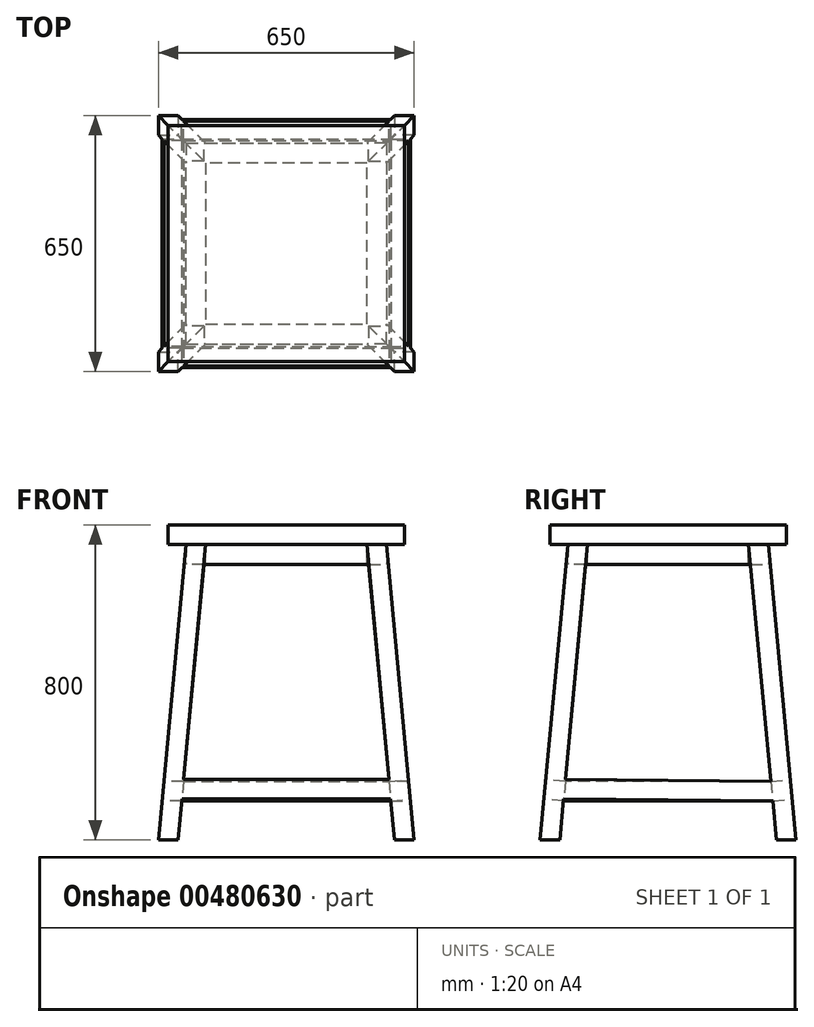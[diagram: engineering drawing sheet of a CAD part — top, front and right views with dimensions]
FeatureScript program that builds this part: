
annotation { "Feature Type Name" : "Feature", "Feature Type Description" : "" }
export const myFeature = defineFeature(function(context is Context, id is Id, definition is map)
    precondition{}
    {
        {
            var Q0;
            Q0=qCreatedBy(makeId("Top.planeOp"),FACE);
            var sketch = newSketch(context, id + "F0", { "sketchPlane" : qUnion([Q0])});
            skLineSegment(sketch, "E0.bottom", {"start": v(-250, 250) * mm, "end": v(250, 250) * mm, "construction": true});
            skLineSegment(sketch, "E0.top", {"start": v(-250, -250) * mm, "end": v(250, -250) * mm, "construction": true});
            skLineSegment(sketch, "E0.left", {"start": v(-250, 250) * mm, "end": v(-250, -250) * mm, "construction": true});
            skLineSegment(sketch, "E0.right", {"start": v(250, 250) * mm, "end": v(250, -250) * mm, "construction": true});
            skPoint(sketch, "E0.middle", {"position": v(0, 0) * mm});
            skLineSegment(sketch, "E1.bottom", {"start": v(-250, -250) * mm, "end": v(-200, -250) * mm});
            skLineSegment(sketch, "E1.top", {"start": v(-250, -200) * mm, "end": v(-200, -200) * mm});
            skLineSegment(sketch, "E1.left", {"start": v(-250, -250) * mm, "end": v(-250, -200) * mm});
            skLineSegment(sketch, "E1.right", {"start": v(-200, -250) * mm, "end": v(-200, -200) * mm});
            skLineSegment(sketch, "E2.bottom", {"start": v(250, -250) * mm, "end": v(200, -250) * mm});
            skLineSegment(sketch, "E2.top", {"start": v(250, -200) * mm, "end": v(200, -200) * mm});
            skLineSegment(sketch, "E2.left", {"start": v(250, -250) * mm, "end": v(250, -200) * mm});
            skLineSegment(sketch, "E2.right", {"start": v(200, -250) * mm, "end": v(200, -200) * mm});
            skLineSegment(sketch, "E3.bottom", {"start": v(250, 250) * mm, "end": v(200, 250) * mm});
            skLineSegment(sketch, "E3.top", {"start": v(250, 200) * mm, "end": v(200, 200) * mm});
            skLineSegment(sketch, "E3.left", {"start": v(250, 250) * mm, "end": v(250, 200) * mm});
            skLineSegment(sketch, "E3.right", {"start": v(200, 250) * mm, "end": v(200, 200) * mm});
            skLineSegment(sketch, "E4.bottom", {"start": v(-250, 250) * mm, "end": v(-200, 250) * mm});
            skLineSegment(sketch, "E4.top", {"start": v(-250, 200) * mm, "end": v(-200, 200) * mm});
            skLineSegment(sketch, "E4.left", {"start": v(-250, 250) * mm, "end": v(-250, 200) * mm});
            skLineSegment(sketch, "E4.right", {"start": v(-200, 250) * mm, "end": v(-200, 200) * mm});
            skSolve(sketch);
        }
        {
            var Q0;
            Q0=qCreatedBy(makeId("Top.planeOp"),FACE);
            cPlane(context, id + "F1", {"entities" : qUnion([Q0]), "cplaneType" : CPlaneType.OFFSET, "offset" : 800 * mm, "oppositeDirection" : true, "width" : 150 * mm, "height" : 150 * mm});
        }
        {
            var Q0;
            Q0=qCreatedBy(id+"F1.planeOp",FACE);
            var sketch = newSketch(context, id + "F2", { "sketchPlane" : qUnion([Q0])});
            skLineSegment(sketch, "E5.bottom", {"start": v(-325, 325) * mm, "end": v(325, 325) * mm, "construction": true});
            skLineSegment(sketch, "E5.top", {"start": v(-325, -325) * mm, "end": v(325, -325) * mm, "construction": true});
            skLineSegment(sketch, "E5.left", {"start": v(-325, 325) * mm, "end": v(-325, -325) * mm, "construction": true});
            skLineSegment(sketch, "E5.right", {"start": v(325, 325) * mm, "end": v(325, -325) * mm, "construction": true});
            skPoint(sketch, "E5.middle", {"position": v(0, 0) * mm});
            skLineSegment(sketch, "E6.bottom", {"start": v(-325, -325) * mm, "end": v(-275, -325) * mm});
            skLineSegment(sketch, "E6.top", {"start": v(-325, -275) * mm, "end": v(-275, -275) * mm});
            skLineSegment(sketch, "E6.left", {"start": v(-325, -325) * mm, "end": v(-325, -275) * mm});
            skLineSegment(sketch, "E6.right", {"start": v(-275, -325) * mm, "end": v(-275, -275) * mm});
            skLineSegment(sketch, "E7.bottom", {"start": v(325, -325) * mm, "end": v(275, -325) * mm});
            skLineSegment(sketch, "E7.top", {"start": v(325, -275) * mm, "end": v(275, -275) * mm});
            skLineSegment(sketch, "E7.left", {"start": v(325, -325) * mm, "end": v(325, -275) * mm});
            skLineSegment(sketch, "E7.right", {"start": v(275, -325) * mm, "end": v(275, -275) * mm});
            skLineSegment(sketch, "E8.bottom", {"start": v(325, 325) * mm, "end": v(275, 325) * mm});
            skLineSegment(sketch, "E8.top", {"start": v(325, 275) * mm, "end": v(275, 275) * mm});
            skLineSegment(sketch, "E8.left", {"start": v(325, 325) * mm, "end": v(325, 275) * mm});
            skLineSegment(sketch, "E8.right", {"start": v(275, 325) * mm, "end": v(275, 275) * mm});
            skLineSegment(sketch, "E9.bottom", {"start": v(-325, 325) * mm, "end": v(-275, 325) * mm});
            skLineSegment(sketch, "E9.top", {"start": v(-325, 275) * mm, "end": v(-275, 275) * mm});
            skLineSegment(sketch, "E9.left", {"start": v(-325, 325) * mm, "end": v(-325, 275) * mm});
            skLineSegment(sketch, "E9.right", {"start": v(-275, 325) * mm, "end": v(-275, 275) * mm});
            skSolve(sketch);
        }
        {
            var Q0;
            Q0=qCreatedBy(makeId("Top.planeOp"),FACE);
            var sketch = newSketch(context, id + "F3", { "sketchPlane" : qUnion([Q0])});
            skLineSegment(sketch, "E10.bottom", {"start": v(-300, 300) * mm, "end": v(300, 300) * mm});
            skLineSegment(sketch, "E10.top", {"start": v(-300, -300) * mm, "end": v(300, -300) * mm});
            skLineSegment(sketch, "E10.left", {"start": v(-300, 300) * mm, "end": v(-300, -300) * mm});
            skLineSegment(sketch, "E10.right", {"start": v(300, 300) * mm, "end": v(300, -300) * mm});
            skPoint(sketch, "E10.middle", {"position": v(0, 0) * mm});
            skSolve(sketch);
        }
        {
            var Q0;
            Q0=makeQuery(id+"F0.imprint","IMPRINT",FACE,{"disambiguationData":[TD([[makeQuery(id+"F0.imprint","IMPRINT",EDGE,{"derivedFrom":sQuery(id+"F0.wireOp",EDGE,"E1.bottom")}),1.0]])]});
            var Q1;
            Q1=makeQuery(id+"F2.imprint","IMPRINT",FACE,{"disambiguationData":[TD([[makeQuery(id+"F2.imprint","IMPRINT",EDGE,{"derivedFrom":sQuery(id+"F2.wireOp",EDGE,"E6.bottom")}),1.0]])]});
            loft(context, id + "F4", {"sheetProfilesArray" : [{ "sheetProfileEntities" : qUnion([Q0]) }, { "sheetProfileEntities" : qUnion([Q1]) }]});
        }
        {
            var Q0;
            Q0=makeQuery(id+"F0.imprint","IMPRINT",FACE,{"disambiguationData":[TD([[makeQuery(id+"F0.imprint","IMPRINT",EDGE,{"derivedFrom":sQuery(id+"F0.wireOp",EDGE,"E2.bottom")}),-1.0]])]});
            var Q1;
            Q1=makeQuery(id+"F2.imprint","IMPRINT",FACE,{"disambiguationData":[TD([[makeQuery(id+"F2.imprint","IMPRINT",EDGE,{"derivedFrom":sQuery(id+"F2.wireOp",EDGE,"E7.bottom")}),-1.0]])]});
            loft(context, id + "F5", {"sheetProfilesArray" : [{ "sheetProfileEntities" : qUnion([Q0]) }, { "sheetProfileEntities" : qUnion([Q1]) }]});
        }
        {
            var Q0;
            Q0=makeQuery(id+"F0.imprint","IMPRINT",FACE,{"disambiguationData":[TD([[makeQuery(id+"F0.imprint","IMPRINT",EDGE,{"derivedFrom":sQuery(id+"F0.wireOp",EDGE,"E4.bottom")}),-1.0]])]});
            var Q1;
            Q1=makeQuery(id+"F2.imprint","IMPRINT",FACE,{"disambiguationData":[TD([[makeQuery(id+"F2.imprint","IMPRINT",EDGE,{"derivedFrom":sQuery(id+"F2.wireOp",EDGE,"E9.bottom")}),-1.0]])]});
            loft(context, id + "F6", {"sheetProfilesArray" : [{ "sheetProfileEntities" : qUnion([Q0]) }, { "sheetProfileEntities" : qUnion([Q1]) }]});
        }
        {
            var Q0;
            Q0=makeQuery(id+"F0.imprint","IMPRINT",FACE,{"disambiguationData":[TD([[makeQuery(id+"F0.imprint","IMPRINT",EDGE,{"derivedFrom":sQuery(id+"F0.wireOp",EDGE,"E3.bottom")}),1.0]])]});
            var Q1;
            Q1=makeQuery(id+"F2.imprint","IMPRINT",FACE,{"disambiguationData":[TD([[makeQuery(id+"F2.imprint","IMPRINT",EDGE,{"derivedFrom":sQuery(id+"F2.wireOp",EDGE,"E8.bottom")}),1.0]])]});
            loft(context, id + "F7", {"sheetProfilesArray" : [{ "sheetProfileEntities" : qUnion([Q0]) }, { "sheetProfileEntities" : qUnion([Q1]) }]});
        }
        {
            var Q0;
            Q0=qSketchRegion(id+"F3",true);
            extrude(context, id + "F8", {"entities" : qUnion([Q0]), "operationType" : NewBodyOperationType.ADD, "oppositeDirection" : true, "depth" : 50 * mm});
        }
        {
            var Q0;
            Q0=makeQuery(id+"F8.opExtrude","CAP_FACE",FACE,{"disambiguationData":[OSD([sQuery(id+"F3.wireOp",EDGE,"E10.bottom"),sQuery(id+"F3.wireOp",EDGE,"E10.top"),sQuery(id+"F3.wireOp",EDGE,"E10.left"),sQuery(id+"F3.wireOp",EDGE,"E10.right")])],"isStart":false});
            var sketch = newSketch(context, id + "F9", { "sketchPlane" : qUnion([Q0])});
            skLineSegment(sketch, "E11", {"start": v(204.69, 204.69) * mm, "end": v(204.69, -204.69) * mm});
            skLineSegment(sketch, "E12", {"start": v(254.69, -204.69) * mm, "end": v(254.69, 204.69) * mm});
            skLineSegment(sketch, "E13", {"start": v(-204.69, -204.69) * mm, "end": v(-204.69, 204.69) * mm});
            skLineSegment(sketch, "E14", {"start": v(-204.69, 204.69) * mm, "end": v(204.69, 204.69) * mm});
            skLineSegment(sketch, "E15", {"start": v(204.69, 254.69) * mm, "end": v(-204.69, 254.69) * mm});
            skLineSegment(sketch, "E16", {"start": v(204.69, -254.69) * mm, "end": v(-204.69, -254.69) * mm});
            skLineSegment(sketch, "E17", {"start": v(-204.69, 254.69) * mm, "end": v(-254.69, 254.69) * mm});
            skLineSegment(sketch, "E18", {"start": v(-254.69, 254.69) * mm, "end": v(-254.69, -254.69) * mm});
            skLineSegment(sketch, "E19", {"start": v(-254.69, -254.69) * mm, "end": v(-204.69, -254.69) * mm});
            skLineSegment(sketch, "E20", {"start": v(204.69, -254.69) * mm, "end": v(254.69, -254.69) * mm});
            skLineSegment(sketch, "E21", {"start": v(254.69, -254.69) * mm, "end": v(254.69, -204.69) * mm});
            skLineSegment(sketch, "E22", {"start": v(254.69, 204.69) * mm, "end": v(254.69, 254.69) * mm});
            skLineSegment(sketch, "E23", {"start": v(254.69, 254.69) * mm, "end": v(204.69, 254.69) * mm});
            skLineSegment(sketch, "E24", {"start": v(204.69, -204.69) * mm, "end": v(-204.69, -204.69) * mm});
            skSolve(sketch);
        }
        {
            var Q0;
            Q0=qSketchRegion(id+"F9",true);
            extrude(context, id + "F10", {"entities" : qUnion([Q0]), "operationType" : NewBodyOperationType.ADD, "depth" : 50 * mm});
        }
        {
            var Q0;
            Q0=qCreatedBy(id+"F1.planeOp",FACE);
            cPlane(context, id + "F11", {"entities" : qUnion([Q0]), "cplaneType" : CPlaneType.OFFSET, "offset" : 80 * mm, "width" : 150 * mm, "height" : 150 * mm});
        }
        {
            var Q0;
            Q0=makeQuery(id+"F6.opLoft","SWEPT_FACE",FACE,{"disambiguationData":[OSD([sQuery(id+"F0.wireOp",EDGE,"E4.top"),sQuery(id+"F0.wireOp",EDGE,"E4.left"),sQuery(id+"F0.wireOp",EDGE,"E4.right"),sQuery(id+"F2.wireOp",EDGE,"E9.top"),sQuery(id+"F2.wireOp",EDGE,"E9.left"),sQuery(id+"F2.wireOp",EDGE,"E9.right")])]});
            var sketch = newSketch(context, id + "F12", { "sketchPlane" : qUnion([Q0])});
            skLineSegment(sketch, "E25", {"start": v(-275, -822.18) * mm, "end": v(-265.7, -722.6) * mm, "construction": true});
            skLineSegment(sketch, "E26", {"start": v(-265.7, -722.6) * mm, "end": v(-261.06, -672.83) * mm});
            skLineSegment(sketch, "E27", {"start": v(-311.06, -672.83) * mm, "end": v(-315.7, -722.6) * mm});
            skLineSegment(sketch, "E28", {"start": v(-315.7, -722.6) * mm, "end": v(-265.7, -722.6) * mm});
            skLineSegment(sketch, "E29", {"start": v(-261.06, -672.83) * mm, "end": v(-311.06, -672.83) * mm});
            skSolve(sketch);
        }
        {
            var Q0;
            Q0=makeQuery(id+"F6.opLoft","SWEPT_FACE",FACE,{"disambiguationData":[OSD([sQuery(id+"F0.wireOp",EDGE,"E4.bottom"),sQuery(id+"F0.wireOp",EDGE,"E4.top"),sQuery(id+"F0.wireOp",EDGE,"E4.right"),sQuery(id+"F2.wireOp",EDGE,"E9.bottom"),sQuery(id+"F2.wireOp",EDGE,"E9.top"),sQuery(id+"F2.wireOp",EDGE,"E9.right")])]});
            var sketch = newSketch(context, id + "F13", { "sketchPlane" : qUnion([Q0])});
            skLineSegment(sketch, "E30", {"start": v(275, -822.18) * mm, "end": v(265.7, -722.6) * mm, "construction": true});
            skLineSegment(sketch, "E31", {"start": v(265.7, -722.6) * mm, "end": v(261.06, -672.83) * mm});
            skLineSegment(sketch, "E32", {"start": v(265.7, -722.6) * mm, "end": v(315.27, -717.98) * mm});
            skLineSegment(sketch, "E33", {"start": v(261.06, -672.83) * mm, "end": v(310.63, -668.2) * mm});
            skLineSegment(sketch, "E34", {"start": v(310.63, -668.2) * mm, "end": v(315.27, -717.98) * mm});
            skSolve(sketch);
        }
        {
            var Q0;
            Q0=makeQuery(id+"F7.opLoft","SWEPT_FACE",FACE,{"disambiguationData":[OSD([sQuery(id+"F0.wireOp",EDGE,"E3.bottom"),sQuery(id+"F0.wireOp",EDGE,"E3.top"),sQuery(id+"F0.wireOp",EDGE,"E3.right"),sQuery(id+"F2.wireOp",EDGE,"E8.bottom"),sQuery(id+"F2.wireOp",EDGE,"E8.top"),sQuery(id+"F2.wireOp",EDGE,"E8.right")])]});
            var sketch = newSketch(context, id + "F14", { "sketchPlane" : qUnion([Q0])});
            skLineSegment(sketch, "E35", {"start": v(-275, -822.18) * mm, "end": v(-265.7, -722.6) * mm, "construction": true});
            skLineSegment(sketch, "E36", {"start": v(-265.7, -722.6) * mm, "end": v(-261.06, -672.83) * mm});
            skLineSegment(sketch, "E37", {"start": v(-261.06, -672.83) * mm, "end": v(-310.63, -668.2) * mm});
            skLineSegment(sketch, "E38", {"start": v(-265.7, -722.6) * mm, "end": v(-315.27, -717.98) * mm});
            skLineSegment(sketch, "E39", {"start": v(-315.27, -717.98) * mm, "end": v(-310.63, -668.2) * mm});
            skSolve(sketch);
        }
        {
            var Q1;
            Q1=makeQuery(id+"F13.imprint","IMPRINT",FACE,{"disambiguationData":[TD([[makeQuery(id+"F13.imprint","IMPRINT",EDGE,{"derivedFrom":sQuery(id+"F13.wireOp",EDGE,"E31")}),1.0]])]});
            var Q2;
            Q2=makeQuery(id+"F14.imprint","IMPRINT",FACE,{"disambiguationData":[TD([[makeQuery(id+"F14.imprint","IMPRINT",EDGE,{"derivedFrom":sQuery(id+"F14.wireOp",EDGE,"E36")}),-1.0]])]});
            loft(context, id + "F15", {"operationType" : NewBodyOperationType.ADD, "sheetProfilesArray" : [{ "sheetProfileEntities" : qUnion([Q1]) }, { "sheetProfileEntities" : qUnion([Q2]) }]});
        }
        {
            var Q0;
            Q0=makeQuery(id+"F4.opLoft","SWEPT_FACE",FACE,{"disambiguationData":[OSD([sQuery(id+"F0.wireOp",EDGE,"E1.top"),sQuery(id+"F0.wireOp",EDGE,"E1.left"),sQuery(id+"F0.wireOp",EDGE,"E1.right"),sQuery(id+"F2.wireOp",EDGE,"E6.top"),sQuery(id+"F2.wireOp",EDGE,"E6.left"),sQuery(id+"F2.wireOp",EDGE,"E6.right")])]});
            var sketch = newSketch(context, id + "F16", { "sketchPlane" : qUnion([Q0])});
            skLineSegment(sketch, "E40", {"start": v(275, -822.18) * mm, "end": v(265.7, -722.6) * mm, "construction": true});
            skLineSegment(sketch, "E41", {"start": v(265.7, -722.6) * mm, "end": v(315.7, -722.6) * mm});
            skLineSegment(sketch, "E42", {"start": v(265.7, -722.6) * mm, "end": v(261.06, -672.83) * mm});
            skLineSegment(sketch, "E43", {"start": v(261.06, -672.83) * mm, "end": v(311.06, -672.83) * mm});
            skLineSegment(sketch, "E44", {"start": v(311.06, -672.83) * mm, "end": v(315.7, -722.6) * mm});
            skSolve(sketch);
        }
        {
            var Q0;
            Q0=makeQuery(id+"F4.opLoft","SWEPT_FACE",FACE,{"disambiguationData":[OSD([sQuery(id+"F0.wireOp",EDGE,"E1.bottom"),sQuery(id+"F0.wireOp",EDGE,"E1.top"),sQuery(id+"F0.wireOp",EDGE,"E1.right"),sQuery(id+"F2.wireOp",EDGE,"E6.bottom"),sQuery(id+"F2.wireOp",EDGE,"E6.top"),sQuery(id+"F2.wireOp",EDGE,"E6.right")])]});
            var sketch = newSketch(context, id + "F17", { "sketchPlane" : qUnion([Q0])});
            skLineSegment(sketch, "E45", {"start": v(-275, -822.18) * mm, "end": v(-265.7, -722.6) * mm, "construction": true});
            skLineSegment(sketch, "E46", {"start": v(-265.7, -722.6) * mm, "end": v(-261.06, -672.83) * mm});
            skLineSegment(sketch, "E47", {"start": v(-265.7, -722.6) * mm, "end": v(-315.27, -717.98) * mm});
            skLineSegment(sketch, "E48", {"start": v(-261.06, -672.83) * mm, "end": v(-310.63, -668.2) * mm});
            skLineSegment(sketch, "E49", {"start": v(-310.63, -668.2) * mm, "end": v(-315.27, -717.98) * mm});
            skSolve(sketch);
        }
        {
            var Q1;
            Q1=makeQuery(id+"F12.imprint","IMPRINT",FACE,{"disambiguationData":[TD([[makeQuery(id+"F12.imprint","IMPRINT",EDGE,{"derivedFrom":sQuery(id+"F12.wireOp",EDGE,"E26")}),-1.0]])]});
            var Q2;
            Q2=makeQuery(id+"F16.imprint","IMPRINT",FACE,{"disambiguationData":[TD([[makeQuery(id+"F16.imprint","IMPRINT",EDGE,{"derivedFrom":sQuery(id+"F16.wireOp",EDGE,"E41")}),1.0]])]});
            loft(context, id + "F18", {"operationType" : NewBodyOperationType.ADD, "sheetProfilesArray" : [{ "sheetProfileEntities" : qUnion([Q1]) }, { "sheetProfileEntities" : qUnion([Q2]) }]});
        }
        {
            var Q0;
            Q0=makeQuery(id+"F5.opLoft","SWEPT_FACE",FACE,{"disambiguationData":[OSD([sQuery(id+"F0.wireOp",EDGE,"E2.bottom"),sQuery(id+"F0.wireOp",EDGE,"E2.top"),sQuery(id+"F0.wireOp",EDGE,"E2.right"),sQuery(id+"F2.wireOp",EDGE,"E7.bottom"),sQuery(id+"F2.wireOp",EDGE,"E7.top"),sQuery(id+"F2.wireOp",EDGE,"E7.right")])]});
            var sketch = newSketch(context, id + "F19", { "sketchPlane" : qUnion([Q0])});
            skLineSegment(sketch, "E50", {"start": v(275, -822.18) * mm, "end": v(265.7, -722.6) * mm, "construction": true});
            skLineSegment(sketch, "E51", {"start": v(265.7, -722.6) * mm, "end": v(261.06, -672.83) * mm});
            skLineSegment(sketch, "E52", {"start": v(265.7, -722.6) * mm, "end": v(315.27, -717.98) * mm});
            skLineSegment(sketch, "E53", {"start": v(261.06, -672.83) * mm, "end": v(310.63, -668.2) * mm});
            skLineSegment(sketch, "E54", {"start": v(310.63, -668.2) * mm, "end": v(315.27, -717.98) * mm});
            skSolve(sketch);
        }
        {
            var Q0;
            Q0=makeQuery(id+"F5.opLoft","SWEPT_FACE",FACE,{"disambiguationData":[OSD([sQuery(id+"F0.wireOp",EDGE,"E2.top"),sQuery(id+"F0.wireOp",EDGE,"E2.left"),sQuery(id+"F0.wireOp",EDGE,"E2.right"),sQuery(id+"F2.wireOp",EDGE,"E7.top"),sQuery(id+"F2.wireOp",EDGE,"E7.left"),sQuery(id+"F2.wireOp",EDGE,"E7.right")])]});
            var sketch = newSketch(context, id + "F20", { "sketchPlane" : qUnion([Q0])});
            skLineSegment(sketch, "E55", {"start": v(-275, -822.18) * mm, "end": v(-265.7, -722.6) * mm, "construction": true});
            skLineSegment(sketch, "E56", {"start": v(-265.7, -722.6) * mm, "end": v(-261.06, -672.83) * mm});
            skLineSegment(sketch, "E57", {"start": v(-265.7, -722.6) * mm, "end": v(-315.27, -717.98) * mm});
            skLineSegment(sketch, "E58", {"start": v(-261.06, -672.83) * mm, "end": v(-310.63, -668.2) * mm});
            skLineSegment(sketch, "E59", {"start": v(-310.63, -668.2) * mm, "end": v(-315.27, -717.98) * mm});
            skSolve(sketch);
        }
        {
            var Q1;
            Q1=makeQuery(id+"F17.imprint","IMPRINT",FACE,{"disambiguationData":[TD([[makeQuery(id+"F17.imprint","IMPRINT",EDGE,{"derivedFrom":sQuery(id+"F17.wireOp",EDGE,"E46")}),-1.0]])]});
            var Q2;
            Q2=makeQuery(id+"F19.imprint","IMPRINT",FACE,{"disambiguationData":[TD([[makeQuery(id+"F19.imprint","IMPRINT",EDGE,{"derivedFrom":sQuery(id+"F19.wireOp",EDGE,"E51")}),1.0]])]});
            loft(context, id + "F21", {"operationType" : NewBodyOperationType.ADD, "sheetProfilesArray" : [{ "sheetProfileEntities" : qUnion([Q1]) }, { "sheetProfileEntities" : qUnion([Q2]) }]});
        }
        {
            var Q0;
            {var subQ0=sQuery(id+"F9.wireOp",EDGE,"E22");var subQ1=sQuery(id+"F9.wireOp",EDGE,"E21");var subQ2=sQuery(id+"F9.wireOp",EDGE,"E12");var subQ3=sQuery(id+"F2.wireOp",EDGE,"E8.left");var subQ4=sQuery(id+"F2.wireOp",EDGE,"E8.top");var subQ6=sQuery(id+"F0.wireOp",EDGE,"E3.left");var subQ7=sQuery(id+"F0.wireOp",EDGE,"E3.top");var subQ9=sQuery(id+"F2.wireOp",EDGE,"E8.right");var subQ16=sQuery(id+"F2.wireOp",EDGE,"E9.right");var subQ17=sQuery(id+"F2.wireOp",EDGE,"E9.top");var subQ20=sQuery(id+"F0.wireOp",EDGE,"E4.right");var subQ21=sQuery(id+"F0.wireOp",EDGE,"E4.top");var subQ24=sQuery(id+"F0.wireOp",EDGE,"E3.right");var subQ25=makeQuery(id+"F7.opLoft","SWEPT_FACE",FACE,{"disambiguationData":[OSD([subQ7,subQ6,subQ24,subQ4,subQ3,subQ9])]});var subQ29=sQuery(id+"F14.wireOp",EDGE,"E37");var subQ30=sQuery(id+"F14.wireOp",EDGE,"E36");var subQ32=sQuery(id+"F13.wireOp",EDGE,"E33");var subQ33=sQuery(id+"F13.wireOp",EDGE,"E31");var subQ34=sQuery(id+"F2.wireOp",EDGE,"E9.left");var subQ35=sQuery(id+"F0.wireOp",EDGE,"E4.left");var subQ36=makeQuery(id+"F6.opLoft","SWEPT_FACE",FACE,{"disambiguationData":[OSD([subQ21,subQ35,subQ20,subQ17,subQ34,subQ16])]});var subQ37=sQuery(id+"F14.wireOp",EDGE,"E38");var subQ38=sQuery(id+"F13.wireOp",EDGE,"E32");var subQ39=makeQuery(id+"F15.opLoft","SWEPT_FACE",FACE,{"disambiguationData":[OSD([subQ7,subQ24,subQ21,subQ20,subQ4,subQ9,subQ17,subQ16,subQ33,subQ38,subQ32,subQ30,subQ29,subQ37])]});Q0=makeQuery(id+"F18.boolean.opBoolean","SPLIT",FACE,{"disambiguationData":[TD([makeQuery(id+"F10.opExtrude","SWEPT_FACE",FACE,{"disambiguationData":[OSD([subQ2,subQ1,subQ0])]})])],"derivedFrom":makeQuery(id+"F15.boolean.opBoolean","MERGE",FACE,{"derivedFrom":[subQ36,subQ25,subQ39]})});}
            var sketch = newSketch(context, id + "F22", { "sketchPlane" : qUnion([Q0])});
            skLineSegment(sketch, "E60", {"start": v(275, -822.18) * mm, "end": v(265.7, -722.6) * mm, "construction": true});
            skLineSegment(sketch, "E61", {"start": v(265.7, -722.6) * mm, "end": v(315.7, -722.6) * mm});
            skLineSegment(sketch, "E62", {"start": v(315.7, -722.6) * mm, "end": v(311.06, -672.83) * mm});
            skLineSegment(sketch, "E63", {"start": v(311.06, -672.83) * mm, "end": v(261.06, -672.83) * mm});
            skLineSegment(sketch, "E64", {"start": v(261.06, -672.83) * mm, "end": v(265.7, -722.6) * mm});
            skSolve(sketch);
        }
        {
            var Q1;
            Q1=makeQuery(id+"F22.imprint","IMPRINT",FACE,{"disambiguationData":[TD([[makeQuery(id+"F22.imprint","IMPRINT",EDGE,{"derivedFrom":sQuery(id+"F22.wireOp",EDGE,"E61")}),1.0]])]});
            var Q2;
            Q2=makeQuery(id+"F20.imprint","IMPRINT",FACE,{"disambiguationData":[TD([[makeQuery(id+"F20.imprint","IMPRINT",EDGE,{"derivedFrom":sQuery(id+"F20.wireOp",EDGE,"E56")}),-1.0]])]});
            loft(context, id + "F23", {"operationType" : NewBodyOperationType.ADD, "sheetProfilesArray" : [{ "sheetProfileEntities" : qUnion([Q1]) }, { "sheetProfileEntities" : qUnion([Q2]) }]});
        }
    });
